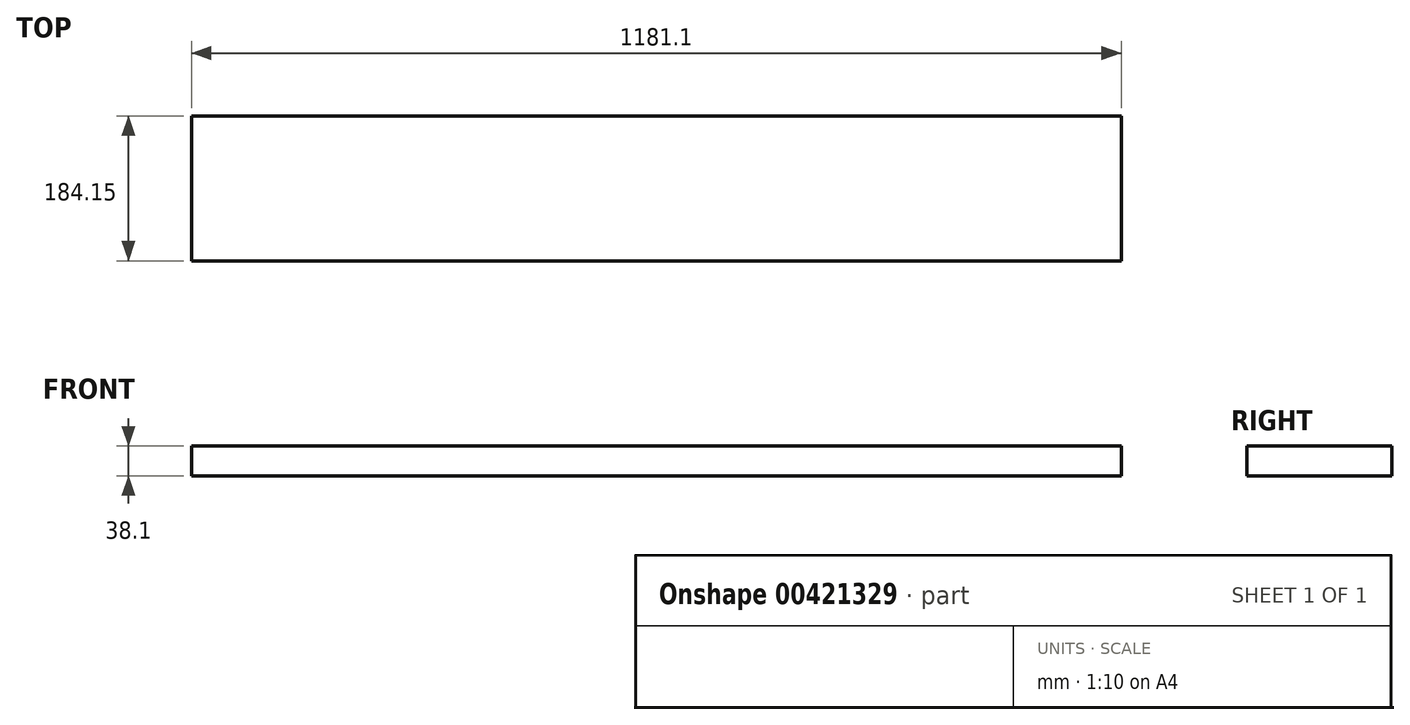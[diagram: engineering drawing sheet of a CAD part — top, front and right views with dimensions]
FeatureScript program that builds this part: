
annotation { "Feature Type Name" : "Feature", "Feature Type Description" : "" }
export const myFeature = defineFeature(function(context is Context, id is Id, definition is map)
    precondition{}
    {
        {
            var Q0;
            Q0=qCreatedBy(makeId("Top.planeOp"),FACE);
            var sketch = newSketch(context, id + "F0", { "sketchPlane" : qUnion([Q0])});
            skLineSegment(sketch, "E0.bottom", {"start": v(-104.48, -41.5) * mm, "end": v(1076.62, -41.5) * mm});
            skLineSegment(sketch, "E0.top", {"start": v(-104.48, 142.64) * mm, "end": v(1076.62, 142.64) * mm});
            skLineSegment(sketch, "E0.left", {"start": v(-104.48, -41.5) * mm, "end": v(-104.48, 142.64) * mm});
            skLineSegment(sketch, "E0.right", {"start": v(1076.62, -41.5) * mm, "end": v(1076.62, 142.64) * mm});
            skSolve(sketch);
        }
        {
            var Q0;
            Q0=makeQuery(id+"F0.imprint","IMPRINT",FACE,{"disambiguationData":[TD([[makeQuery(id+"F0.imprint","IMPRINT",EDGE,{"derivedFrom":sQuery(id+"F0.wireOp",EDGE,"E0.bottom")}),1.0]])]});
            extrude(context, id + "F1", {"entities" : qUnion([Q0]), "depth" : 38.1 * mm});
        }
    });
